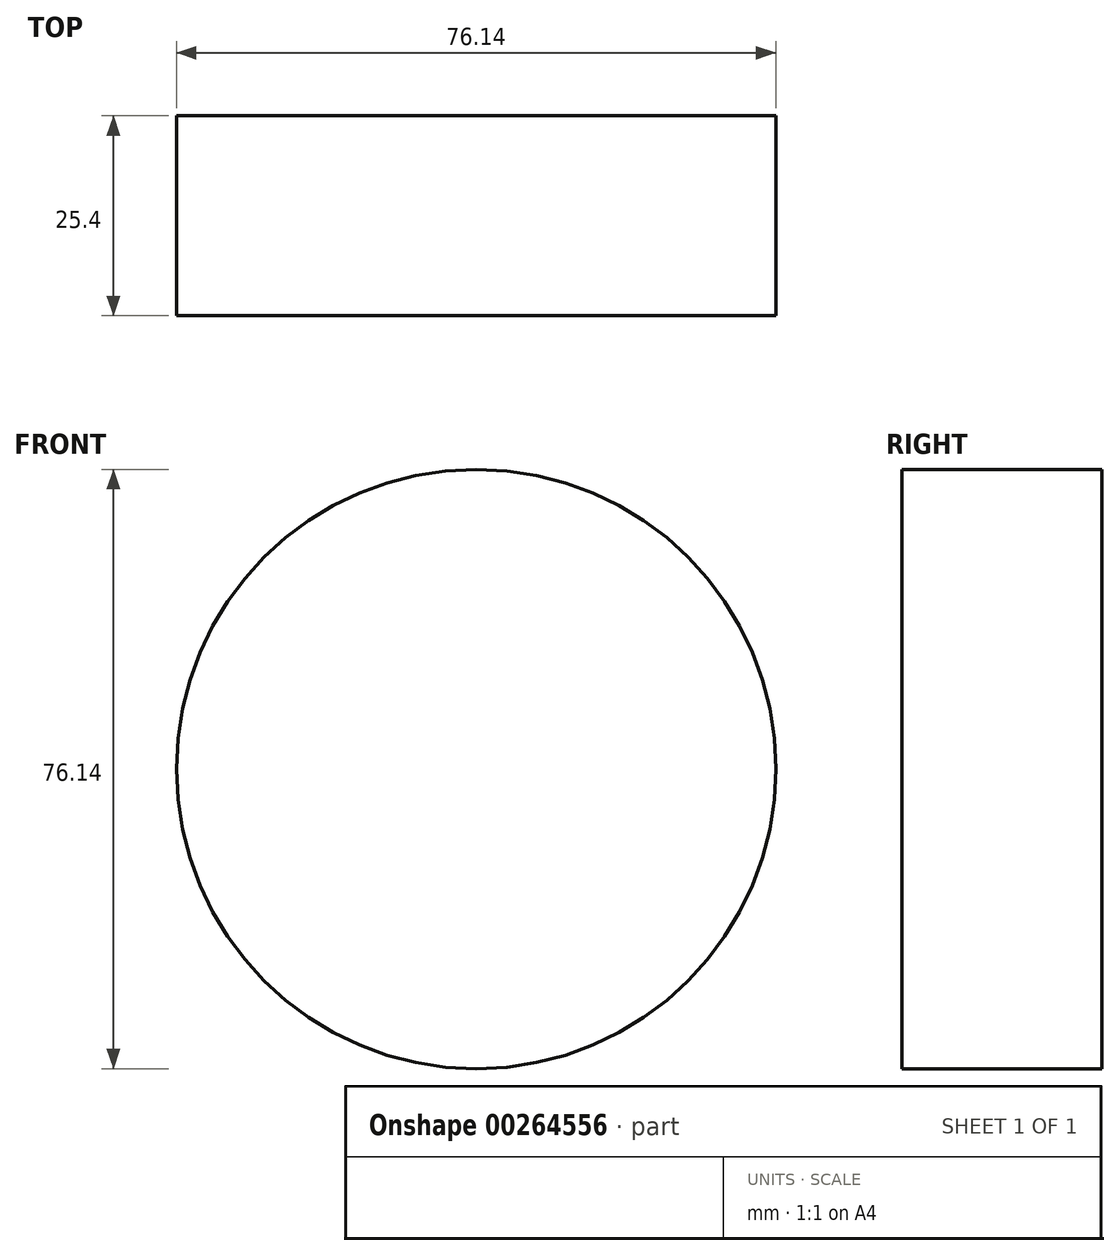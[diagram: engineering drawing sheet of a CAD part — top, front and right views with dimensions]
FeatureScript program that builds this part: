
annotation { "Feature Type Name" : "Feature", "Feature Type Description" : "" }
export const myFeature = defineFeature(function(context is Context, id is Id, definition is map)
    precondition{}
    {
        {
            var Q0;
            Q0=qCreatedBy(makeId("Front.planeOp"),FACE);
            var sketch = newSketch(context, id + "F0", { "sketchPlane" : qUnion([Q0])});
            skCircle(sketch, "E0", {"center": v(0, 0) * mm, "radius": 38.07 * mm});
            skSolve(sketch);
        }
        {
            var Q0;
            Q0 = qSketchRegion(id + "F0", true);
            extrude(context, id + "F1", {"entities" : qUnion([Q0]), "depth" : 25.4 * mm});
        }
    });
